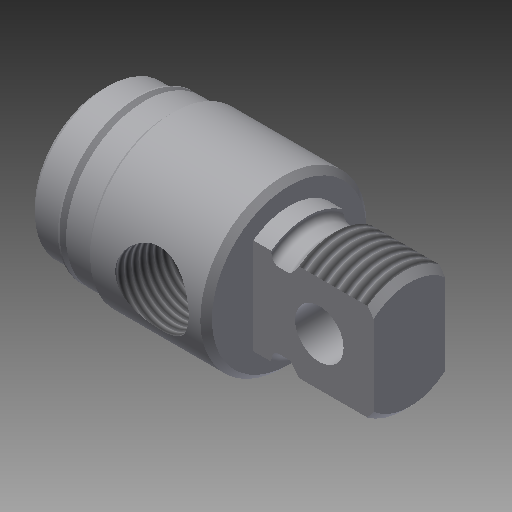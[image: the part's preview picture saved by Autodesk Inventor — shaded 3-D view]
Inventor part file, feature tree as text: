
AUTODESK INVENTOR PART (.ipt)
format: ipt  version: 2019 (Build 230136000, 136)  size: 349,696 bytes
history: native  units: in
note: dims shown in document units (in); Inventor stores cm internally (conversion verified against a paired STEP export)
features: other x154, sketch x7, revolve x4, thread x2, extrude x2, hole x1
ambient origin geometry x8: Origin, YZ Plane, XZ Plane, XY Plane, X Axis, Y Axis, Z Axis, Center Point
bodies: Solid1 (feature_tree)
feature tree (170):
  revolve  "Revolution1"  Angle=360.0deg
  revolve  "Revolution2"  [1 undecoded]
  thread  "Thread1"  [1 undecoded]
  extrude  "Extrusion1"  TaperAngle=360.0deg  [1 undecoded]
  hole  "Hole1"  [1 undecoded]
  revolve  "Revolution3"  [1 undecoded]
  thread  "Thread2"  [1 undecoded]
  revolve  "Revolution4"  [1 undecoded]
  extrude  "Extrusion2"  [1 undecoded]
  other  "1_XY"
  other  "1_YZ"
  other  "1_ZX"
  other  "1_X"
  other  "1_Y"
  other  "1_Z"
  other  "1_Center"
  other  "c1_XY"
  other  "c1_YZ"
  other  "c1_ZX"
  other  "c1_X"
  other  "c1_Y"
  other  "c1_Z"
  other  "c1_Center"
  other  "c2_XY"
  other  "c2_YZ"
  other  "c2_ZX"
  other  "c2_X"
  other  "c2_Y"
  other  "c2_Z"
  other  "c2_Center"
  other  "cc1_XY"
  other  "cc1_YZ"
  other  "cc1_ZX"
  other  "cc1_X"
  other  "cc1_Y"
  other  "cc1_Z"
  other  "cc1_Center"
  other  "cc2_XY"
  other  "cc2_YZ"
  other  "cc2_ZX"
  other  "cc2_X"
  other  "cc2_Y"
  other  "cc2_Z"
  other  "cc2_Center"
  other  "lovra1_XY"
  other  "lovra1_YZ"
  other  "lovra1_ZX"
  other  "lovra1_X"
  other  "lovra1_Y"
  other  "lovra1_Z"
  other  "lovra1_Center"
  other  "lovra2_XY"
  other  "lovra2_YZ"
  other  "lovra2_ZX"
  other  "lovra2_X"
  other  "lovra2_Y"
  other  "lovra2_Z"
  other  "lovra2_Center"
  other  "lovra21_XY"
  other  "lovra21_YZ"
  other  "lovra21_ZX"
  other  "lovra21_X"
  other  "lovra21_Y"
  other  "lovra21_Z"
  other  "lovra21_Center"
  other  "lovra22_XY"
  other  "lovra22_YZ"
  other  "lovra22_ZX"
  other  "lovra22_X"
  other  "lovra22_Y"
  other  "lovra22_Z"
  other  "lovra22_Center"
  other  "lovra3_XY"
  other  "lovra3_YZ"
  other  "lovra3_ZX"
  other  "lovra3_X"
  other  "lovra3_Y"
  other  "lovra3_Z"
  other  "lovra3_Center"
  other  "olen_XY"
  other  "olen_YZ"
  other  "olen_ZX"
  other  "olen_X"
  other  "olen_Y"
  other  "olen_Z"
  other  "olen_Center"
  other  "p1_XY"
  other  "p1_YZ"
  other  "p1_ZX"
  other  "p1_X"
  other  "p1_Y"
  other  "p1_Z"
  other  "p1_Center"
  other  "p2_XY"
  other  "p2_YZ"
  other  "p2_ZX"
  other  "p2_X"
  other  "p2_Y"
  other  "p2_Z"
  other  "p2_Center"
  other  "port_XY"
  other  "port_YZ"
  other  "port_ZX"
  other  "port_X"
  other  "port_Y"
  other  "port_Z"
  other  "port_Center"
  other  "port2_XY"
  other  "port2_YZ"
  other  "port2_ZX"
  other  "port2_X"
  other  "port2_Y"
  other  "port2_Z"
  other  "port2_Center"
  other  "thd1_XY"
  other  "thd1_YZ"
  other  "thd1_ZX"
  other  "thd1_X"
  other  "thd1_Y"
  other  "thd1_Z"
  other  "thd1_Center"
  other  "thd2_XY"
  other  "thd2_YZ"
  other  "thd2_ZX"
  other  "thd2_X"
  other  "thd2_Y"
  other  "thd2_Z"
  other  "thd2_Center"
  other  "to_mounting_bracket_XY"
  other  "to_mounting_bracket_YZ"
  other  "to_mounting_bracket_ZX"
  other  "to_mounting_bracket_X"
  other  "to_mounting_bracket_Y"
  other  "to_mounting_bracket_Z"
  other  "to_mounting_bracket_Center"
  other  "to_nut_XY"
  other  "to_nut_YZ"
  other  "to_nut_ZX"
  other  "to_nut_X"
  other  "to_nut_Y"
  other  "to_nut_Z"
  other  "to_nut_Center"
  other  "to_pin_XY"
  other  "to_pin_YZ"
  other  "to_pin_ZX"
  other  "to_pin_X"
  other  "to_pin_Y"
  other  "to_pin_Z"
  other  "to_pin_Center"
  other  "to_screw_XY"
  other  "to_screw_YZ"
  other  "to_screw_ZX"
  other  "to_screw_X"
  other  "to_screw_Y"
  other  "to_screw_Z"
  other  "to_screw_Center"
  other  "to_tube_XY"
  other  "to_tube_YZ"
  other  "to_tube_ZX"
  other  "to_tube_X"
  other  "to_tube_Y"
  other  "to_tube_Z"
  other  "to_tube_Center"
  sketch  "Sketch_8"  dims[d2=0.3547in d3=0.0in d4=0.625in d5=0.0in]
  sketch  "Sketch_15"  dims[d14=0.3021in d15=0.0in d16=360.0deg]
  sketch  "Sketch_9"  dims[d6=0.312in d7=0.75in d8=0.375in d9=0.25in d10=0.5635in d11=0.9284in d12=120.0deg d13=360.0deg]
  sketch  "Sketch4"  dims[d0=360.0deg d1=360.0deg]
  sketch  "Sketch_68"
  sketch  "Sketch_24"  dims[d17=0.5587in d18=0.0in]
  sketch  "Sketch_43"  dims[d19=0.0in d20=0.0in d21=0.0in d22=0.0in d23=0.0in d24=0.0in d25=0.0in d26=0.0in]
note: 8 required parameter values undecoded (feature->parameter linkage not recoverable at this tier; creation-order binding heuristic only, values carry confidence <= 0.55)